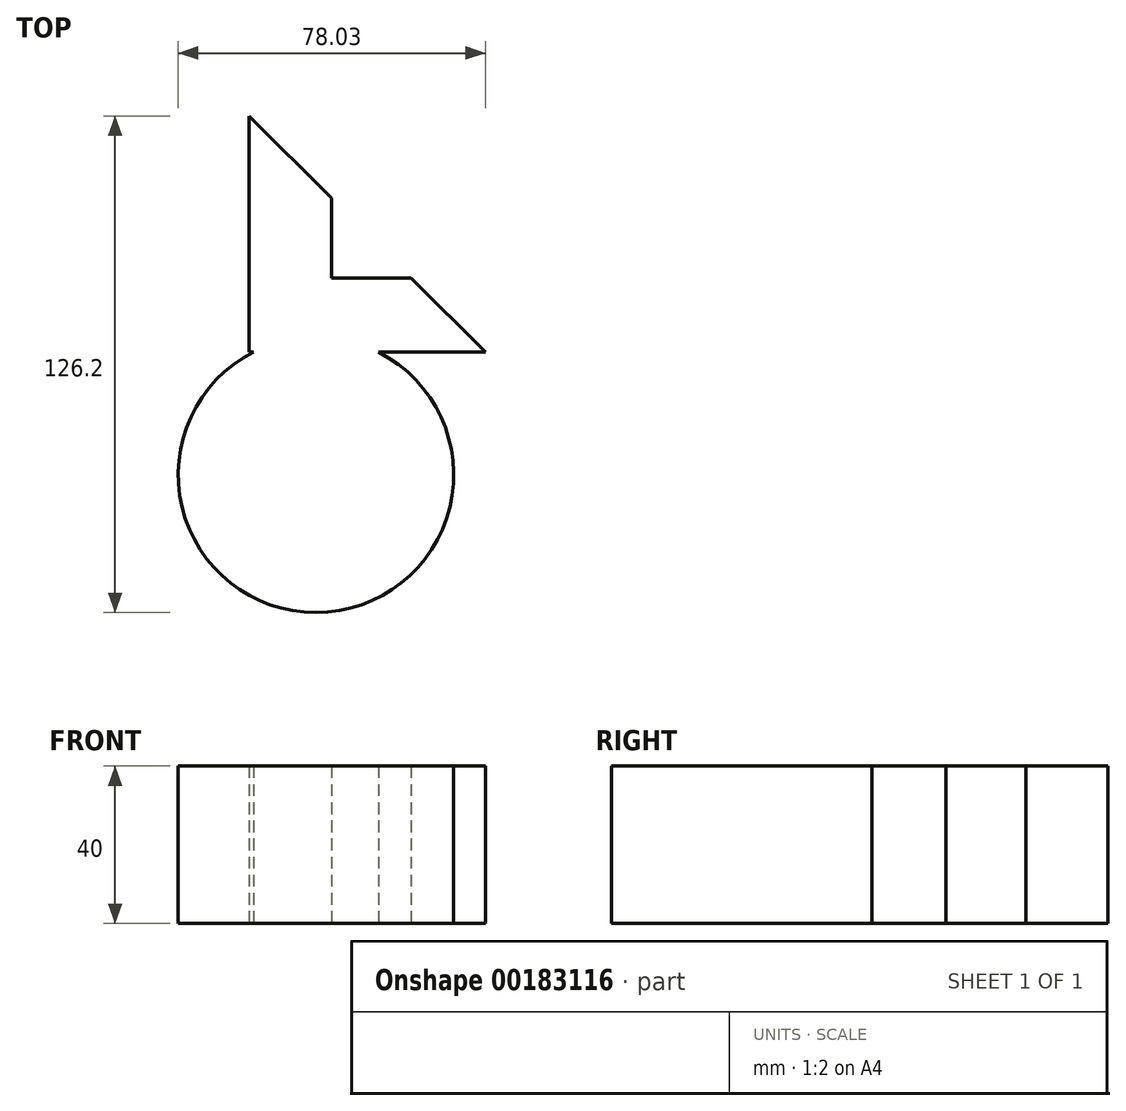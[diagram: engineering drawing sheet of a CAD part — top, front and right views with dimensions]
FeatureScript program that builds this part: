
annotation { "Feature Type Name" : "Feature", "Feature Type Description" : "" }
export const myFeature = defineFeature(function(context is Context, id is Id, definition is map)
    precondition{}
    {
        {
            var Q0;
            Q0=qCreatedBy(makeId("Top.planeOp"),FACE);
            var sketch = newSketch(context, id + "F0", { "sketchPlane" : qUnion([Q0])});
            skLineSegment(sketch, "E0.bottom", {"start": v(-56.06, 36.14) * mm, "end": v(-36.06, 36.14) * mm});
            skLineSegment(sketch, "E0.top", {"start": v(-56.06, -23.86) * mm, "end": v(3.94, -23.86) * mm});
            skLineSegment(sketch, "E0.left", {"start": v(-56.06, 36.14) * mm, "end": v(-56.06, -23.86) * mm});
            skLineSegment(sketch, "E0.right", {"start": v(3.94, -3.58) * mm, "end": v(3.94, -23.86) * mm});
            skLineSegment(sketch, "E1", {"start": v(8.48, 60) * mm, "end": v(8.48, 0) * mm});
            skLineSegment(sketch, "E2", {"start": v(8.48, 0) * mm, "end": v(68.48, 0) * mm});
            skLineSegment(sketch, "E3", {"start": v(68.48, 0) * mm, "end": v(49.67, 18.8) * mm});
            skCircle(sketch, "E4", {"center": v(25.45, -31.2) * mm, "radius": 35 * mm});
            skLineSegment(sketch, "E5.top", {"start": v(-36.06, 0) * mm, "end": v(3.94, 0) * mm});
            skLineSegment(sketch, "E5.left", {"start": v(-36.06, 36.14) * mm, "end": v(-36.06, 0) * mm});
            skLineSegment(sketch, "E6.top", {"start": v(29.38, 18.8) * mm, "end": v(49.67, 18.8) * mm});
            skLineSegment(sketch, "E6.left", {"start": v(29.38, 39.1) * mm, "end": v(29.38, 18.8) * mm});
            skLineSegment(sketch, "E7.trimOffspring", {"start": v(29.38, 39.1) * mm, "end": v(8.48, 60) * mm});
            skSolve(sketch);
        }
        {
            var Q0;
            Q0 = qSketchRegion(id + "F0", true);
            extrude(context, id + "F1", {"entities" : qUnion([Q0]), "depth" : 40 * mm});
        }
    });
